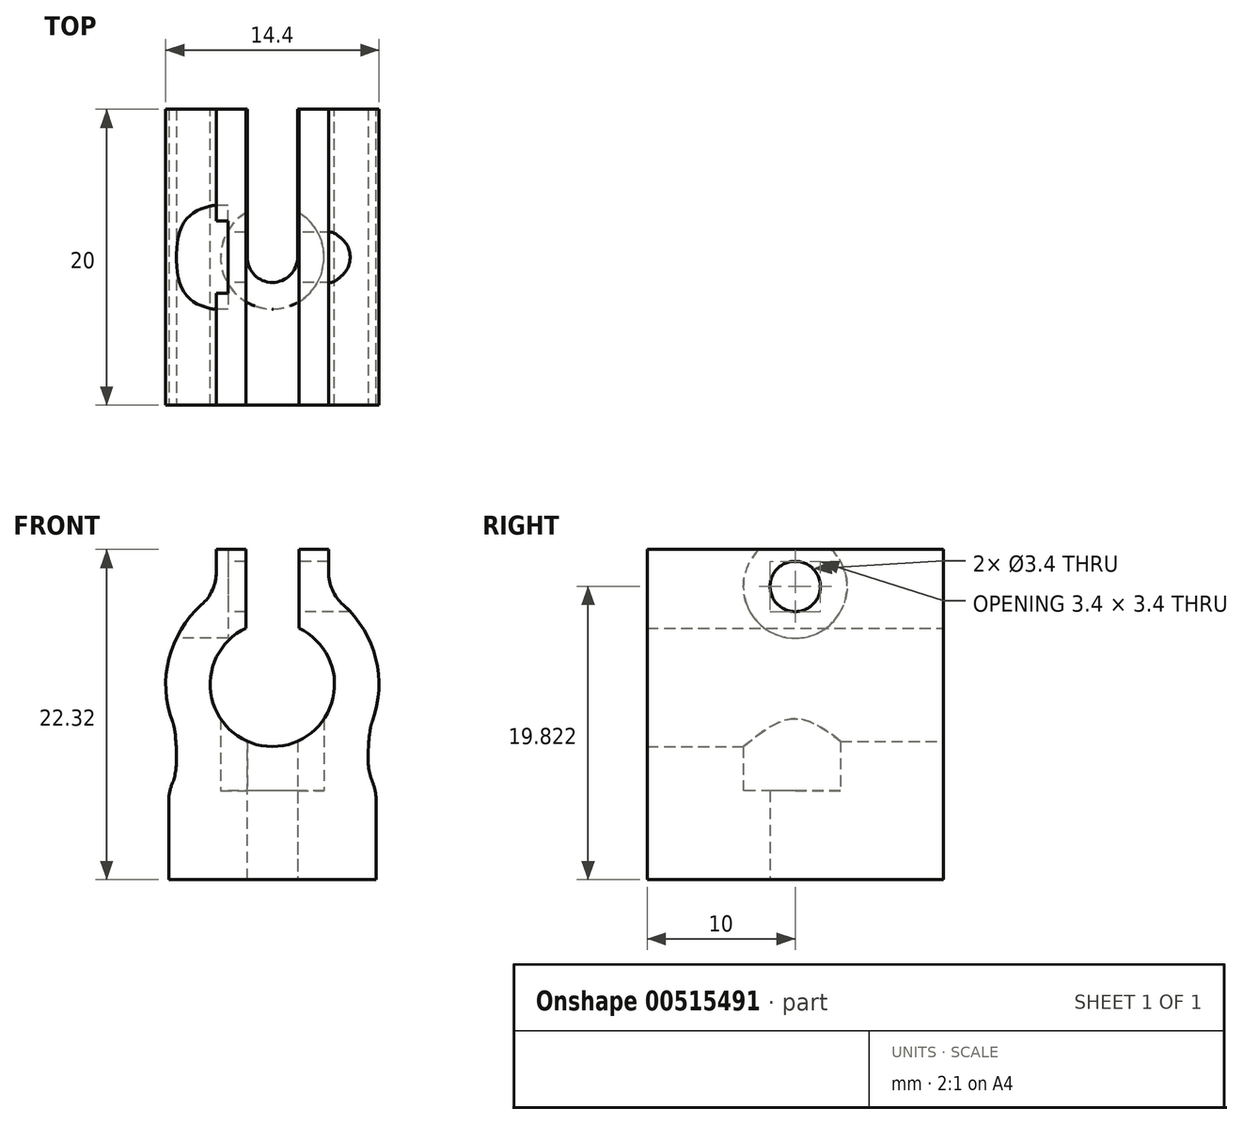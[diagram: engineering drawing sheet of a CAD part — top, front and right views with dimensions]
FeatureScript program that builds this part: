
annotation { "Feature Type Name" : "Feature", "Feature Type Description" : "" }
export const myFeature = defineFeature(function(context is Context, id is Id, definition is map)
    precondition{}
    {
        {
            var Q0;
            Q0=qCreatedBy(makeId("Front.planeOp"),FACE);
            var sketch = newSketch(context, id + "F0", { "sketchPlane" : qUnion([Q0])});
            skArc(sketch, "E0", {"start": v(-1.79, 3.8) * mm, "mid": v(0, -4.2) * mm, "end": v(1.79, 3.8) * mm});
            skArc(sketch, "E1", {"start": v(-3.79, 6.12) * mm, "mid": v(-6.86, 2.19) * mm, "end": v(-6.64, -2.8) * mm});
            skLineSegment(sketch, "E2", {"start": v(3.79, 9.12) * mm, "end": v(3.79, 6.12) * mm});
            skLineSegment(sketch, "E3", {"start": v(-1.79, 9.12) * mm, "end": v(-1.79, 3.8) * mm});
            skLineSegment(sketch, "E4", {"start": v(1.79, 9.12) * mm, "end": v(1.79, 3.8) * mm});
            skLineSegment(sketch, "E5", {"start": v(-1.79, 9.12) * mm, "end": v(-3.79, 9.12) * mm});
            skLineSegment(sketch, "E6", {"start": v(-3.79, 6.12) * mm, "end": v(-3.79, 9.12) * mm});
            skLineSegment(sketch, "E7", {"start": v(1.79, 9.12) * mm, "end": v(3.79, 9.12) * mm});
            skLineSegment(sketch, "E8", {"start": v(-7, -7.2) * mm, "end": v(-7, -13.2) * mm});
            skLineSegment(sketch, "E9", {"start": v(-7, -13.2) * mm, "end": v(7, -13.2) * mm});
            skLineSegment(sketch, "E10", {"start": v(7, -7.2) * mm, "end": v(7, -13.2) * mm});
            skPoint(sketch, "E11.orphan", {"position": v(9.08, -13.2) * mm});
            skFitSpline(sketch, "E12", {"points": [v(-7, -7.2) * mm, v(-6.5, -5.54) * mm, v(-6.64, -2.8) * mm, v(-6.64, -2.77) * mm], "startDerivative": vector(1.57, 3.06) * mm, "endDerivative": vector(-0.17, 0.18) * mm});
            skFitSpline(sketch, "E13", {"points": [v(7, -7.2) * mm, v(6.5, -5.54) * mm, v(6.64, -2.8) * mm], "startDerivative": vector(-1.44, 3.48) * mm, "endDerivative": vector(0.64, 5.26) * mm});
            skArc(sketch, "E14.trimOffspring", {"start": v(6.64, -2.8) * mm, "mid": v(6.86, 2.19) * mm, "end": v(3.79, 6.12) * mm});
            skLineSegment(sketch, "E15", {"start": v(-1.7, -4.2) * mm, "end": v(-1.7, -3.84) * mm});
            skLineSegment(sketch, "E16", {"start": v(-1.7, -4.2) * mm, "end": v(-1.7, -13.2) * mm});
            skLineSegment(sketch, "E17", {"start": v(1.7, -4.2) * mm, "end": v(1.7, -3.84) * mm});
            skLineSegment(sketch, "E18", {"start": v(1.7, -4.2) * mm, "end": v(1.7, -13.2) * mm});
            skPoint(sketch, "E19.start.orphan", {"position": v(0, -4.2) * mm});
            skLineSegment(sketch, "E20", {"start": v(0, -4.2) * mm, "end": v(1.7, -4.2) * mm, "construction": true});
            skLineSegment(sketch, "E21", {"start": v(0, -4.2) * mm, "end": v(-1.7, -4.2) * mm, "construction": true});
            skSolve(sketch);
        }
        {
            var Q0;
            Q0=qSketchRegion(id+"F0",true);
            extrude(context, id + "F1", {"entities" : qUnion([Q0]), "depth" : 20 * mm});
        }
        {
            var Q0;
            Q0=makeQuery(id+"F1.opExtrude","SWEPT_FACE",FACE,{"disambiguationData":[OSD([sQuery(id+"F0.wireOp",EDGE,"E8")])]});
            var sketch = newSketch(context, id + "F2", { "sketchPlane" : qUnion([Q0])});
            skLineSegment(sketch, "E22", {"start": v(10, -13.2) * mm, "end": v(10, 6.62) * mm, "construction": true});
            skCircle(sketch, "E23", {"center": v(10, 6.62) * mm, "radius": 1.7 * mm});
            skCircle(sketch, "E24", {"center": v(10, 6.62) * mm, "radius": 3.5 * mm});
            skSolve(sketch);
        }
        {
            var Q0;
            Q0=makeQuery(id+"F2.imprint","IMPRINT",FACE,{"disambiguationData":[TD([[makeQuery(id+"F2.imprint","IMPRINT",EDGE,{"derivedFrom":sQuery(id+"F2.wireOp",EDGE,"E23")}),-1.0]])]});
            extrude(context, id + "F3", {"entities" : qUnion([Q0]), "operationType" : NewBodyOperationType.REMOVE, "oppositeDirection" : true, "depth" : 4 * mm});
        }
        {
            var Q0;
            Q0=makeQuery(id+"F2.imprint","IMPRINT",FACE,{"disambiguationData":[TD([[makeQuery(id+"F2.imprint","IMPRINT",EDGE,{"derivedFrom":sQuery(id+"F2.wireOp",EDGE,"E23")}),1.0]])]});
            extrude(context, id + "F4", {"entities" : qUnion([Q0]), "operationType" : NewBodyOperationType.REMOVE, "oppositeDirection" : true, "depth" : 25 * mm});
        }
        {
            var Q0;
            Q0=makeQuery(id+"F1.opExtrude","SWEPT_EDGE",EDGE,{"disambiguationData":[OSD([sQuery(id+"F0.wireOp",EDGE,"E1"),sQuery(id+"F0.wireOp",EDGE,"E12")])]});
            var Q1;
            Q1=makeQuery(id+"F1.opExtrude","SWEPT_EDGE",EDGE,{"disambiguationData":[OSD([sQuery(id+"F0.wireOp",EDGE,"E13"),sQuery(id+"F0.wireOp",EDGE,"E14.trimOffspring")])]});
            var Q2;
            Q2=makeQuery(id+"F1.opExtrude","SWEPT_EDGE",EDGE,{"disambiguationData":[OSD([sQuery(id+"F0.wireOp",EDGE,"E8"),sQuery(id+"F0.wireOp",EDGE,"E12")])]});
            var Q3;
            Q3=makeQuery(id+"F1.opExtrude","SWEPT_EDGE",EDGE,{"disambiguationData":[OSD([sQuery(id+"F0.wireOp",EDGE,"E10"),sQuery(id+"F0.wireOp",EDGE,"E13")])]});
            var Q4;
            {var subQ0=sQuery(id+"F0.wireOp",EDGE,"E14.trimOffspring");var subQ1=sQuery(id+"F0.wireOp",EDGE,"E2");Q4=makeQuery(id+"F4.boolean.opBoolean","SPLIT",EDGE,{"disambiguationData":[TD([makeQuery(id+"F1.opExtrude","CAP_FACE",FACE,{"disambiguationData":[OSD([sQuery(id+"F0.wireOp",EDGE,"E0"),sQuery(id+"F0.wireOp",EDGE,"E1"),subQ1,sQuery(id+"F0.wireOp",EDGE,"E3"),sQuery(id+"F0.wireOp",EDGE,"E4"),sQuery(id+"F0.wireOp",EDGE,"E5"),sQuery(id+"F0.wireOp",EDGE,"E6"),sQuery(id+"F0.wireOp",EDGE,"E7"),sQuery(id+"F0.wireOp",EDGE,"E8"),sQuery(id+"F0.wireOp",EDGE,"E9"),sQuery(id+"F0.wireOp",EDGE,"E10"),sQuery(id+"F0.wireOp",EDGE,"E12"),sQuery(id+"F0.wireOp",EDGE,"E13"),subQ0])],"isStart":false})])],"derivedFrom":makeQuery(id+"F1.opExtrude","SWEPT_EDGE",EDGE,{"disambiguationData":[OSD([subQ1,subQ0])]})});}
            var Q5;
            {var subQ0=sQuery(id+"F0.wireOp",EDGE,"E14.trimOffspring");var subQ1=sQuery(id+"F0.wireOp",EDGE,"E2");Q5=makeQuery(id+"F4.boolean.opBoolean","SPLIT",EDGE,{"disambiguationData":[TD([makeQuery(id+"F1.opExtrude","CAP_FACE",FACE,{"disambiguationData":[OSD([sQuery(id+"F0.wireOp",EDGE,"E0"),sQuery(id+"F0.wireOp",EDGE,"E1"),subQ1,sQuery(id+"F0.wireOp",EDGE,"E3"),sQuery(id+"F0.wireOp",EDGE,"E4"),sQuery(id+"F0.wireOp",EDGE,"E5"),sQuery(id+"F0.wireOp",EDGE,"E6"),sQuery(id+"F0.wireOp",EDGE,"E7"),sQuery(id+"F0.wireOp",EDGE,"E8"),sQuery(id+"F0.wireOp",EDGE,"E9"),sQuery(id+"F0.wireOp",EDGE,"E10"),sQuery(id+"F0.wireOp",EDGE,"E12"),sQuery(id+"F0.wireOp",EDGE,"E13"),subQ0])],"isStart":true})])],"derivedFrom":makeQuery(id+"F1.opExtrude","SWEPT_EDGE",EDGE,{"disambiguationData":[OSD([subQ1,subQ0])]})});}
            var Q6;
            {var subQ0=sQuery(id+"F0.wireOp",EDGE,"E6");var subQ1=sQuery(id+"F0.wireOp",EDGE,"E1");Q6=makeQuery(id+"F3.boolean.opBoolean","SPLIT",EDGE,{"disambiguationData":[TD([makeQuery(id+"F1.opExtrude","CAP_FACE",FACE,{"disambiguationData":[OSD([sQuery(id+"F0.wireOp",EDGE,"E0"),subQ1,sQuery(id+"F0.wireOp",EDGE,"E2"),sQuery(id+"F0.wireOp",EDGE,"E3"),sQuery(id+"F0.wireOp",EDGE,"E4"),sQuery(id+"F0.wireOp",EDGE,"E5"),subQ0,sQuery(id+"F0.wireOp",EDGE,"E7"),sQuery(id+"F0.wireOp",EDGE,"E8"),sQuery(id+"F0.wireOp",EDGE,"E9"),sQuery(id+"F0.wireOp",EDGE,"E10"),sQuery(id+"F0.wireOp",EDGE,"E12"),sQuery(id+"F0.wireOp",EDGE,"E13"),sQuery(id+"F0.wireOp",EDGE,"E14.trimOffspring")])],"isStart":true})])],"derivedFrom":makeQuery(id+"F1.opExtrude","SWEPT_EDGE",EDGE,{"disambiguationData":[OSD([subQ1,subQ0])]})});}
            var Q7;
            {var subQ0=sQuery(id+"F0.wireOp",EDGE,"E6");var subQ1=sQuery(id+"F0.wireOp",EDGE,"E1");Q7=makeQuery(id+"F3.boolean.opBoolean","SPLIT",EDGE,{"disambiguationData":[TD([makeQuery(id+"F1.opExtrude","CAP_FACE",FACE,{"disambiguationData":[OSD([sQuery(id+"F0.wireOp",EDGE,"E0"),subQ1,sQuery(id+"F0.wireOp",EDGE,"E2"),sQuery(id+"F0.wireOp",EDGE,"E3"),sQuery(id+"F0.wireOp",EDGE,"E4"),sQuery(id+"F0.wireOp",EDGE,"E5"),subQ0,sQuery(id+"F0.wireOp",EDGE,"E7"),sQuery(id+"F0.wireOp",EDGE,"E8"),sQuery(id+"F0.wireOp",EDGE,"E9"),sQuery(id+"F0.wireOp",EDGE,"E10"),sQuery(id+"F0.wireOp",EDGE,"E12"),sQuery(id+"F0.wireOp",EDGE,"E13"),sQuery(id+"F0.wireOp",EDGE,"E14.trimOffspring")])],"isStart":false})])],"derivedFrom":makeQuery(id+"F1.opExtrude","SWEPT_EDGE",EDGE,{"disambiguationData":[OSD([subQ1,subQ0])]})});}
            fillet(context, id + "F5", {"entities" : qUnion([Q0, Q1, Q2, Q3, Q4, Q5, Q6, Q7]), "radius" : 3 * mm, "tangentPropagation" : true, "allowEdgeOverflow" : false});
        }
        {
            var Q0;
            Q0=makeQuery(id+"F1.opExtrude","SWEPT_FACE",FACE,{"disambiguationData":[OSD([sQuery(id+"F0.wireOp",EDGE,"E9")])]});
            var sketch = newSketch(context, id + "F6", { "sketchPlane" : qUnion([Q0])});
            skLineSegment(sketch, "E25", {"start": v(-7, 10) * mm, "end": v(0, 10) * mm, "construction": true});
            skCircle(sketch, "E26", {"center": v(0, 10) * mm, "radius": 1.7 * mm});
            skCircle(sketch, "E27", {"center": v(0, 10) * mm, "radius": 3.5 * mm});
            skSolve(sketch);
        }
        {
            var Q0;
            Q0=makeQuery(id+"F6.imprint","IMPRINT",FACE,{"disambiguationData":[TD([[makeQuery(id+"F6.imprint","IMPRINT",EDGE,{"derivedFrom":sQuery(id+"F6.wireOp",EDGE,"E26")}),-1.0]])]});
            extrude(context, id + "F7", {"entities" : qUnion([Q0]), "operationType" : NewBodyOperationType.REMOVE, "oppositeDirection" : true, "depth" : 12 * mm});
        }
        {
            var Q0;
            Q0=makeQuery(id+"F7.boolean.opBoolean","SPLIT",FACE,{"disambiguationData":[TD([makeQuery(id+"F7.opExtrude","SWEPT_FACE",FACE,{"disambiguationData":[OSD([sQuery(id+"F6.wireOp",EDGE,"E26")])]})])],"derivedFrom":makeQuery(id+"F1.opExtrude","SWEPT_FACE",FACE,{"disambiguationData":[OSD([sQuery(id+"F0.wireOp",EDGE,"E9")])]})});
            extrude(context, id + "F8", {"entities" : qUnion([Q0]), "operationType" : NewBodyOperationType.REMOVE, "oppositeDirection" : true, "depth" : 12 * mm});
        }
        {
            var Q0;
            Q0=makeQuery(id+"F6.imprint","IMPRINT",FACE,{"disambiguationData":[TD([[makeQuery(id+"F6.imprint","IMPRINT",EDGE,{"derivedFrom":sQuery(id+"F6.wireOp",EDGE,"E26")}),-1.0]])]});
            extrude(context, id + "F9", {"entities" : qUnion([Q0]), "operationType" : NewBodyOperationType.ADD, "oppositeDirection" : true, "depth" : 6 * mm});
        }
        {
            var Q0;
            {var subQ0=sQuery(id+"F0.wireOp",EDGE,"E15");Q0=makeQuery(id+"F0.imprint","IMPRINT",FACE,{"disambiguationData":[TD([[makeQuery(id+"F0.imprint","IMPRINT",EDGE,{"derivedFrom":subQ0}),-1.0]])]});}
            extrude(context, id + "F10", {"entities" : qUnion([Q0]), "operationType" : NewBodyOperationType.REMOVE, "depth" : 10 * mm});
        }
    });
